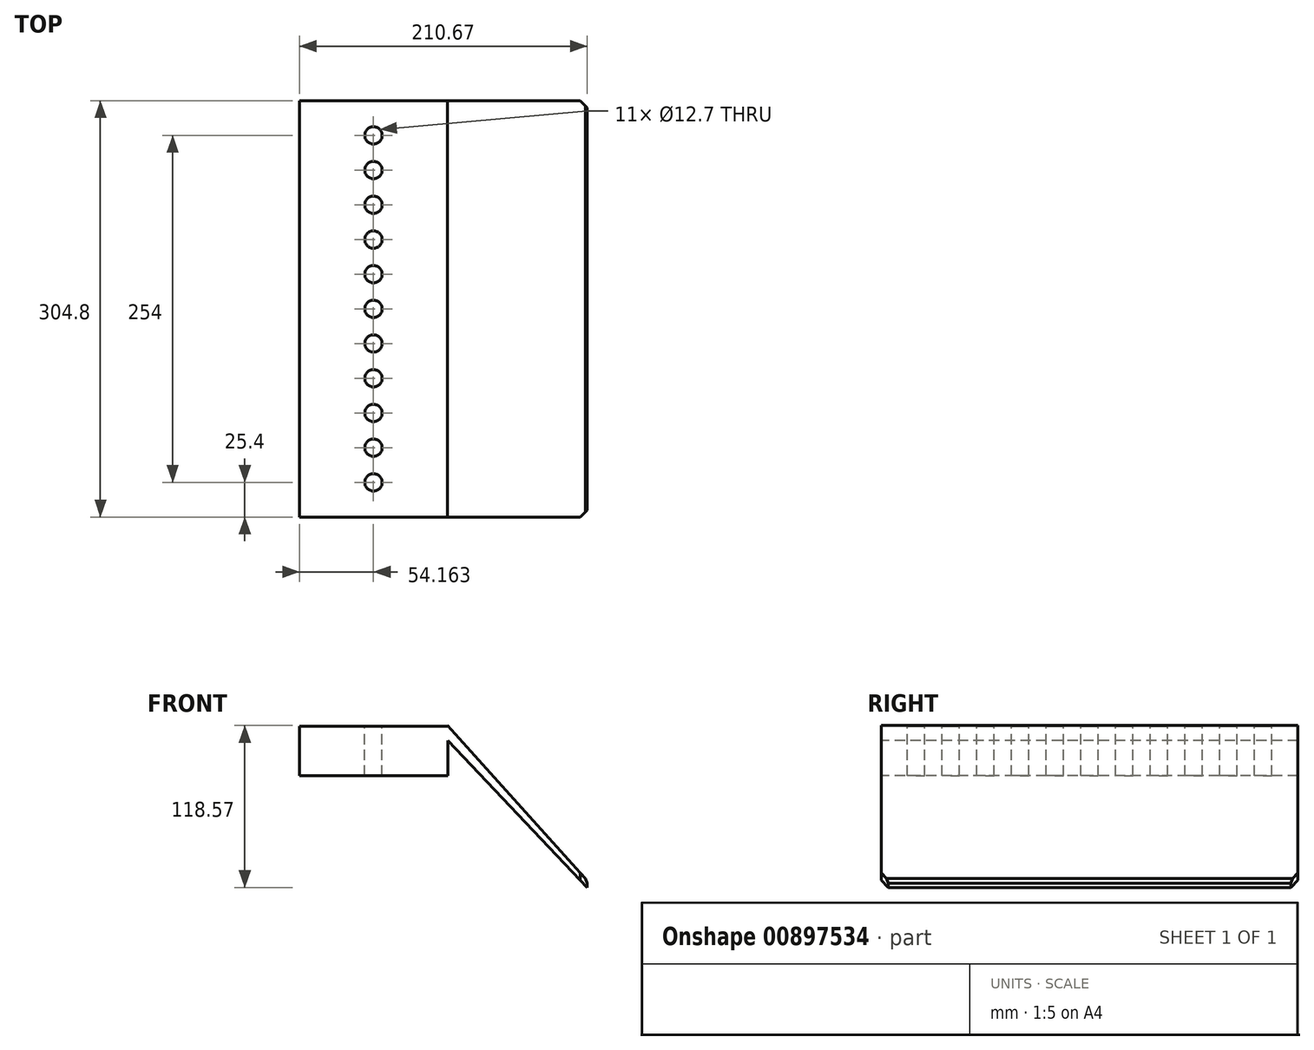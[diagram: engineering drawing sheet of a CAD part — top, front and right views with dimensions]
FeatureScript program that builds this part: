
annotation { "Feature Type Name" : "Feature", "Feature Type Description" : "" }
export const myFeature = defineFeature(function(context is Context, id is Id, definition is map)
    precondition{}
    {
        {
            var Q0;
            Q0=qCreatedBy(makeId("Front.planeOp"),FACE);
            var sketch = newSketch(context, id + "F0", { "sketchPlane" : qUnion([Q0])});
            skLineSegment(sketch, "E0", {"start": v(0, 0) * mm, "end": v(0, 36.24) * mm});
            skLineSegment(sketch, "E1", {"start": v(0, 36.24) * mm, "end": v(108.7, 36.24) * mm});
            skLineSegment(sketch, "E2", {"start": v(0, 0) * mm, "end": v(108.7, 0) * mm});
            skLineSegment(sketch, "E3", {"start": v(108.7, 36.24) * mm, "end": v(108.7, 36.24) * mm});
            skLineSegment(sketch, "E4", {"start": v(108.7, 36.24) * mm, "end": v(108.7, 0) * mm});
            skSolve(sketch);
        }
        {
            var Q0;
            Q0=makeQuery(id+"F0.imprint","IMPRINT",FACE,{"disambiguationData":[TD([[makeQuery(id+"F0.imprint","IMPRINT",EDGE,{"derivedFrom":sQuery(id+"F0.wireOp",EDGE,"E0")}),-1.0]])]});
            extrude(context, id + "F1", {"entities" : qUnion([Q0]), "oppositeDirection" : true, "depth" : 304.8 * mm, "offsetDistance" : 25.4 * mm});
        }
        {
            var Q0;
            Q0=makeQuery(id+"F0.imprint","IMPRINT",FACE,{"disambiguationData":[TD([[makeQuery(id+"F0.imprint","IMPRINT",EDGE,{"derivedFrom":sQuery(id+"F0.wireOp",EDGE,"E0")}),-1.0]])]});
            var sketch = newSketch(context, id + "F2", { "sketchPlane" : qUnion([Q0])});
            skLineSegment(sketch, "E5.bottom", {"start": v(108.33, 36.81) * mm, "end": v(108.33, 36.81) * mm});
            skLineSegment(sketch, "E6", {"start": v(108.33, 36.81) * mm, "end": v(210.67, -76.65) * mm});
            skLineSegment(sketch, "E7", {"start": v(210.67, -76.65) * mm, "end": v(210.67, -81.76) * mm});
            skLineSegment(sketch, "E8", {"start": v(108.33, 26.14) * mm, "end": v(210.67, -81.76) * mm});
            skLineSegment(sketch, "E9", {"start": v(108.33, 36.81) * mm, "end": v(108.33, 26.14) * mm});
            skSolve(sketch);
        }
        {
            var Q0;
            {var subQ1=sQuery(id+"F2.wireOp",EDGE,"E6");Q0=makeQuery(id+"F2.imprint","IMPRINT",FACE,{"disambiguationData":[TD([[makeQuery(id+"F2.imprint","IMPRINT",EDGE,{"derivedFrom":subQ1}),-1.0]])]});}
            extrude(context, id + "F3", {"entities" : qUnion([Q0]), "operationType" : NewBodyOperationType.ADD, "oppositeDirection" : true, "depth" : 304.8 * mm, "offsetDistance" : 25.4 * mm});
        }
        {
            var Q0;
            Q0=makeQuery(id+"F3.opExtrude","CAP_EDGE",EDGE,{"disambiguationData":[OSD([sQuery(id+"F2.wireOp",EDGE,"E7")])],"isStart":true});
            var Q1;
            Q1=makeQuery(id+"F3.opExtrude","SWEPT_EDGE",EDGE,{"disambiguationData":[OSD([sQuery(id+"F2.wireOp",EDGE,"E6"),sQuery(id+"F2.wireOp",EDGE,"E7")])]});
            var Q2;
            Q2=makeQuery(id+"F3.opExtrude","CAP_EDGE",EDGE,{"disambiguationData":[OSD([sQuery(id+"F2.wireOp",EDGE,"E7")])],"isStart":false});
            chamfer(context, id + "F4", {"entities" : qUnion([Q0, Q1, Q2]), "width" : 5.08 * mm, "tangentPropagation" : true});
        }
        {
            var Q0;
            Q0=makeQuery(id+"F1.opExtrude","SWEPT_FACE",FACE,{"disambiguationData":[OSD([sQuery(id+"F0.wireOp",EDGE,"E1")])]});
            var sketch = newSketch(context, id + "F5", { "sketchPlane" : qUnion([Q0])});
            skPoint(sketch, "E10", {"position": v(54.16, 152.4) * mm});
            skPoint(sketch, "E11", {"position": v(54.16, 228.6) * mm});
            skLineSegment(sketch, "E12", {"start": v(54.16, 304.8) * mm, "end": v(54.16, 0) * mm});
            skLineSegment(sketch, "E13", {"start": v(54.16, 304.8) * mm, "end": v(54.16, 279.4) * mm});
            skLineSegment(sketch, "E14", {"start": v(54.16, 279.4) * mm, "end": v(54.16, 254) * mm});
            skLineSegment(sketch, "E15", {"start": v(54.16, 228.6) * mm, "end": v(54.16, 193.98) * mm});
            skLineSegment(sketch, "E16", {"start": v(54.16, 304.8) * mm, "end": v(54.16, 177.8) * mm});
            skLineSegment(sketch, "E17", {"start": v(54.16, 152.4) * mm, "end": v(54.16, 203.16) * mm});
            skLineSegment(sketch, "E18", {"start": v(54.16, 152.4) * mm, "end": v(54.16, 127.09) * mm});
            skPoint(sketch, "E19", {"position": v(54.16, 279.4) * mm});
            skPoint(sketch, "E20", {"position": v(54.16, 254) * mm});
            skPoint(sketch, "E21", {"position": v(54.16, 127.09) * mm});
            skPoint(sketch, "E22", {"position": v(54.16, 177.8) * mm});
            skPoint(sketch, "E23", {"position": v(54.16, 203.16) * mm});
            skLineSegment(sketch, "E24", {"start": v(54.16, 127.09) * mm, "end": v(54.16, 0) * mm});
            skLineSegment(sketch, "E25", {"start": v(54.16, 0) * mm, "end": v(54.16, 25.4) * mm});
            skLineSegment(sketch, "E26", {"start": v(54.16, 0) * mm, "end": v(54.16, 50.8) * mm});
            skLineSegment(sketch, "E27", {"start": v(54.16, 0) * mm, "end": v(54.16, 101.6) * mm});
            skLineSegment(sketch, "E28", {"start": v(54.16, 0) * mm, "end": v(54.16, 76.2) * mm});
            skPoint(sketch, "E29", {"position": v(54.16, 76.2) * mm});
            skPoint(sketch, "E30", {"position": v(54.16, 101.6) * mm});
            skPoint(sketch, "E31", {"position": v(54.16, 50.8) * mm});
            skPoint(sketch, "E32", {"position": v(54.16, 25.4) * mm});
            skSolve(sketch);
        }
        {
            var Q0;
            Q0=sQuery(id+"F5.wireOp",VERTEX,"E11");
            var Q1;
            Q1=sQuery(id+"F5.wireOp",VERTEX,"E10");
            var Q2;
            Q2=sQuery(id+"F5.wireOp",VERTEX,"6fcaa2b0-d192-4574-8ac1-c19318e7b35d");
            var Q3;
            Q3=sQuery(id+"F5.wireOp",VERTEX,"E19");
            var Q4;
            Q4=sQuery(id+"F5.wireOp",VERTEX,"E20");
            var Q5;
            Q5=sQuery(id+"F5.wireOp",VERTEX,"E22");
            var Q6;
            Q6=sQuery(id+"F5.wireOp",VERTEX,"E23");
            var Q7;
            Q7=sQuery(id+"F5.wireOp",VERTEX,"E21");
            var Q8;
            Q8=sQuery(id+"F5.wireOp",VERTEX,"E27.end");
            var Q9;
            Q9=sQuery(id+"F5.wireOp",VERTEX,"E26.end");
            var Q10;
            Q10=sQuery(id+"F5.wireOp",VERTEX,"E25.end");
            var Q11;
            Q11=sQuery(id+"F5.wireOp",VERTEX,"E29");
            var Q12;
            Q12=makeQuery(id+"F1.opExtrude","SWEPT_BODY",BODY,{"disambiguationData":[OSD([sQuery(id+"F0.wireOp",EDGE,"E0"),sQuery(id+"F0.wireOp",EDGE,"E1"),sQuery(id+"F0.wireOp",EDGE,"E2"),sQuery(id+"F0.wireOp",EDGE,"E4")])]});
            hole(context, id + "F6", {"style" : HoleStyle.SIMPLE, "endStyle" : HoleEndStyle.THROUGH, "holeDiameter" : 12.7 * mm, "majorDiameter" : 6.35 * mm, "isTappedThrough" : true, "tappedDepth" : 12.7 * mm, "tapClearance" : 3, "locations" : qUnion([Q0, Q1, Q2, Q3, Q4, Q5, Q6, Q7, Q8, Q9, Q10, Q11]), "scope" : qUnion([Q12])});
        }
    });
